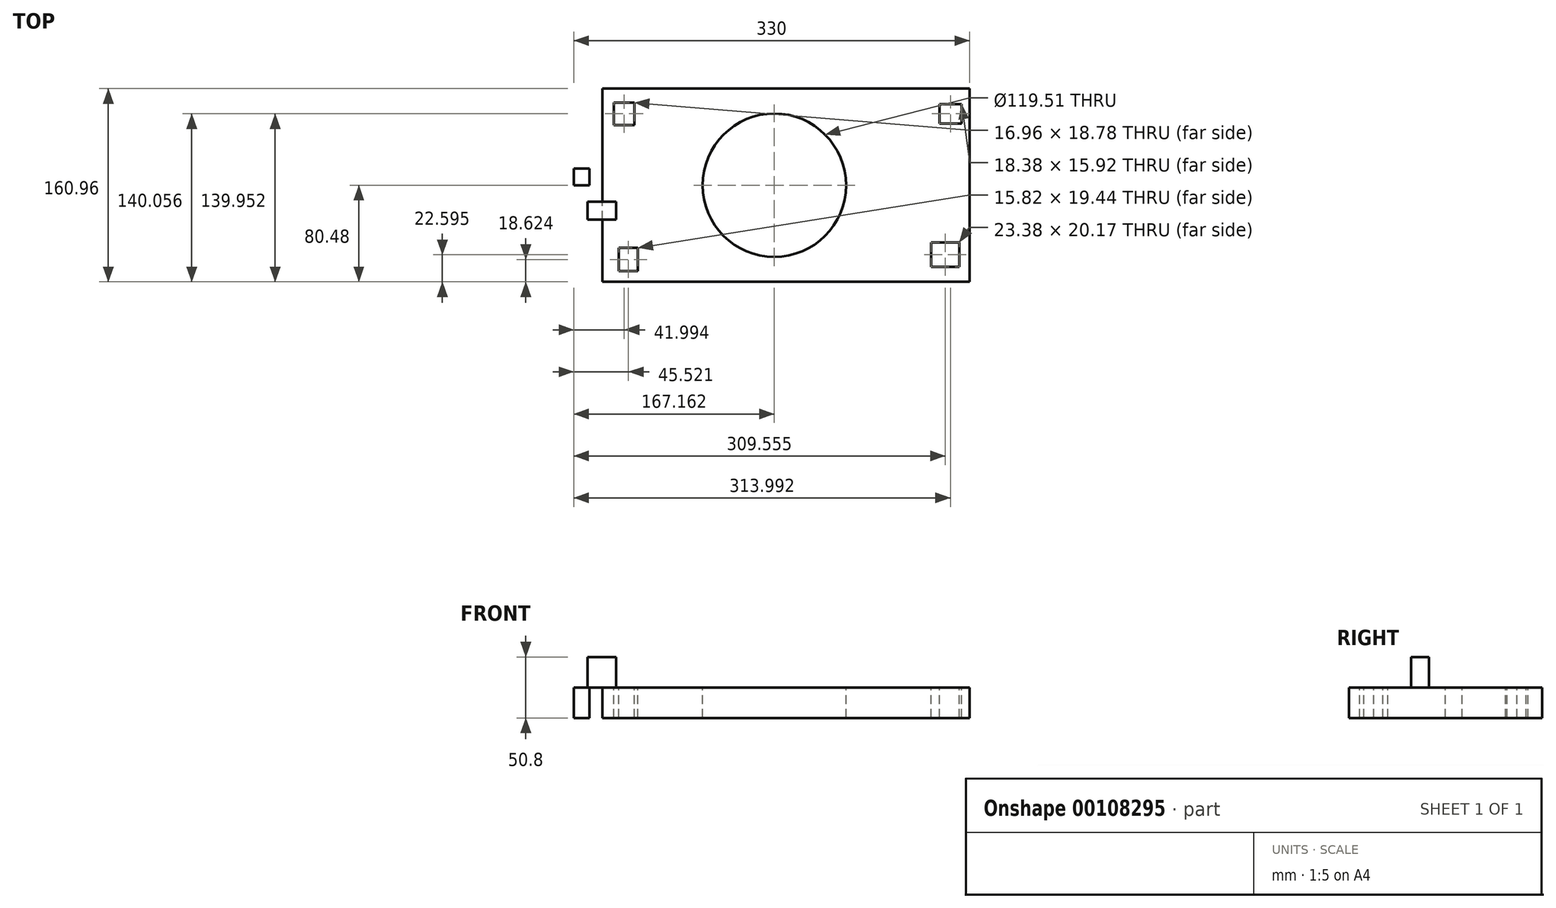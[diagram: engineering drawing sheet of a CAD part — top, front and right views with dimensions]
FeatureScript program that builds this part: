
annotation { "Feature Type Name" : "Feature", "Feature Type Description" : "" }
export const myFeature = defineFeature(function(context is Context, id is Id, definition is map)
    precondition{}
    {
        {
            var Q0;
            Q0=qCreatedBy(makeId("Top.planeOp"),FACE);
            var sketch = newSketch(context, id + "F0", { "sketchPlane" : qUnion([Q0])});
            skLineSegment(sketch, "E0.bottom", {"start": v(153.1, -80.48) * mm, "end": v(-153.1, -80.48) * mm});
            skLineSegment(sketch, "E0.top", {"start": v(153.1, 80.48) * mm, "end": v(-153.1, 80.48) * mm});
            skLineSegment(sketch, "E0.left", {"start": v(153.1, -80.48) * mm, "end": v(153.1, 80.48) * mm});
            skLineSegment(sketch, "E0.right", {"start": v(-153.1, -80.48) * mm, "end": v(-153.1, 80.48) * mm});
            skPoint(sketch, "E0.middle", {"position": v(0, 0) * mm});
            skSolve(sketch);
        }
        {
            var Q0;
            Q0 = qSketchRegion(id + "F0", true);
            extrude(context, id + "F1", {"entities" : qUnion([Q0]), "depth" : 25.4 * mm});
        }
        {
            var Q0;
            Q0=makeQuery(id+"F1.opExtrude","CAP_FACE",FACE,{"disambiguationData":[OSD([sQuery(id+"F0.wireOp",EDGE,"E0.bottom"),sQuery(id+"F0.wireOp",EDGE,"E0.top"),sQuery(id+"F0.wireOp",EDGE,"E0.left"),sQuery(id+"F0.wireOp",EDGE,"E0.right")])],"isStart":false});
            var sketch = newSketch(context, id + "F2", { "sketchPlane" : qUnion([Q0])});
            skLineSegment(sketch, "E1.bottom", {"start": v(-143.39, 68.97) * mm, "end": v(-126.42, 68.97) * mm});
            skLineSegment(sketch, "E1.top", {"start": v(-143.39, 50.19) * mm, "end": v(-126.42, 50.19) * mm});
            skLineSegment(sketch, "E1.left", {"start": v(-143.39, 68.97) * mm, "end": v(-143.39, 50.19) * mm});
            skLineSegment(sketch, "E1.right", {"start": v(-126.42, 68.97) * mm, "end": v(-126.42, 50.19) * mm});
            skLineSegment(sketch, "E2.bottom", {"start": v(127.9, 67.43) * mm, "end": v(146.28, 67.43) * mm});
            skLineSegment(sketch, "E2.top", {"start": v(127.9, 51.51) * mm, "end": v(146.28, 51.51) * mm});
            skLineSegment(sketch, "E2.left", {"start": v(127.9, 67.43) * mm, "end": v(127.9, 51.51) * mm});
            skLineSegment(sketch, "E2.right", {"start": v(146.28, 67.43) * mm, "end": v(146.28, 51.51) * mm});
            skLineSegment(sketch, "E3.bottom", {"start": v(-139.29, -52.14) * mm, "end": v(-123.47, -52.14) * mm});
            skLineSegment(sketch, "E3.top", {"start": v(-139.29, -71.58) * mm, "end": v(-123.47, -71.58) * mm});
            skLineSegment(sketch, "E3.left", {"start": v(-139.29, -52.14) * mm, "end": v(-139.29, -71.58) * mm});
            skLineSegment(sketch, "E3.right", {"start": v(-123.47, -52.14) * mm, "end": v(-123.47, -71.58) * mm});
            skSolve(sketch);
        }
        {
            var Q0;
            Q0 = qSketchRegion(id + "F2", true);
            extrude(context, id + "F3", {"entities" : qUnion([Q0]), "operationType" : NewBodyOperationType.REMOVE, "oppositeDirection" : true, "depth" : 25.4 * mm});
        }
        {
            var Q0;
            Q0=makeQuery(id+"F1.opExtrude","CAP_FACE",FACE,{"disambiguationData":[OSD([sQuery(id+"F0.wireOp",EDGE,"E0.bottom"),sQuery(id+"F0.wireOp",EDGE,"E0.top"),sQuery(id+"F0.wireOp",EDGE,"E0.left"),sQuery(id+"F0.wireOp",EDGE,"E0.right")])],"isStart":false});
            var sketch = newSketch(context, id + "F4", { "sketchPlane" : qUnion([Q0])});
            skLineSegment(sketch, "E4.bottom", {"start": v(120.96, -47.8) * mm, "end": v(144.35, -47.8) * mm});
            skLineSegment(sketch, "E4.top", {"start": v(120.96, -67.97) * mm, "end": v(144.35, -67.97) * mm});
            skLineSegment(sketch, "E4.left", {"start": v(120.96, -47.8) * mm, "end": v(120.96, -67.97) * mm});
            skLineSegment(sketch, "E4.right", {"start": v(144.35, -47.8) * mm, "end": v(144.35, -67.97) * mm});
            skSolve(sketch);
        }
        {
            var Q0;
            Q0 = qSketchRegion(id + "F4", true);
            extrude(context, id + "F5", {"entities" : qUnion([Q0]), "operationType" : NewBodyOperationType.REMOVE, "oppositeDirection" : true, "depth" : 25.4 * mm});
        }
        {
            var Q0;
            Q0=makeQuery(id+"F1.opExtrude","CAP_FACE",FACE,{"disambiguationData":[OSD([sQuery(id+"F0.wireOp",EDGE,"E0.bottom"),sQuery(id+"F0.wireOp",EDGE,"E0.top"),sQuery(id+"F0.wireOp",EDGE,"E0.left"),sQuery(id+"F0.wireOp",EDGE,"E0.right")])],"isStart":false});
            var sketch = newSketch(context, id + "F6", { "sketchPlane" : qUnion([Q0])});
            skLineSegment(sketch, "E5", {"start": v(-139.29, -61.86) * mm, "end": v(-165.4, -13.75) * mm});
            skLineSegment(sketch, "E6.bottom", {"start": v(-165.4, -13.75) * mm, "end": v(-141.78, -13.75) * mm});
            skLineSegment(sketch, "E6.top", {"start": v(-165.4, -28.68) * mm, "end": v(-141.78, -28.68) * mm});
            skLineSegment(sketch, "E6.left", {"start": v(-165.4, -13.75) * mm, "end": v(-165.4, -28.68) * mm});
            skLineSegment(sketch, "E6.right", {"start": v(-141.78, -13.75) * mm, "end": v(-141.78, -28.68) * mm});
            skSolve(sketch);
        }
        {
            var Q0;
            Q0 = qSketchRegion(id + "F6", true);
            extrude(context, id + "F7", {"entities" : qUnion([Q0]), "operationType" : NewBodyOperationType.ADD, "depth" : 25.4 * mm});
        }
        {
            var Q0;
            {var subQ4=makeQuery(id+"F1.opExtrude","CAP_EDGE",EDGE,{"disambiguationData":[OSD([sQuery(id+"F0.wireOp",EDGE,"E0.bottom")])],"isStart":false});Q0=makeQuery(id+"F6.imprint","IMPRINT",FACE,{"disambiguationData":[TD([[makeQuery(id+"F6.imprint","IMPRINT",EDGE,{"derivedFrom":subQ4}),-1.0]])]});}
            var sketch = newSketch(context, id + "F8", { "sketchPlane" : qUnion([Q0])});
            skLineSegment(sketch, "E7.bottom", {"start": v(-176.9, 13.9) * mm, "end": v(-163.88, 13.9) * mm});
            skLineSegment(sketch, "E7.top", {"start": v(-176.9, 0) * mm, "end": v(-163.88, 0) * mm});
            skLineSegment(sketch, "E7.left", {"start": v(-176.9, 13.9) * mm, "end": v(-176.9, 0) * mm});
            skLineSegment(sketch, "E7.right", {"start": v(-163.88, 13.9) * mm, "end": v(-163.88, 0) * mm});
            skSolve(sketch);
        }
        {
            var Q0;
            Q0 = qSketchRegion(id + "F8", true);
            extrude(context, id + "F9", {"entities" : qUnion([Q0]), "operationType" : NewBodyOperationType.ADD, "oppositeDirection" : true, "depth" : 25.4 * mm});
        }
        {
            var Q0;
            Q0=qCreatedBy(makeId("Right.planeOp"),FACE);
            var sketch = newSketch(context, id + "F10", { "sketchPlane" : qUnion([Q0])});
            skLineSegment(sketch, "E8.bottom", {"start": v(195.7, -224.48) * mm, "end": v(352.54, -224.48) * mm});
            skLineSegment(sketch, "E8.top", {"start": v(195.7, -96.3) * mm, "end": v(352.54, -96.3) * mm});
            skLineSegment(sketch, "E8.left", {"start": v(195.7, -224.48) * mm, "end": v(195.7, -96.3) * mm});
            skLineSegment(sketch, "E8.right", {"start": v(352.54, -224.48) * mm, "end": v(352.54, -96.3) * mm});
            skLineSegment(sketch, "E9.bottom", {"start": v(-353.36, 280.55) * mm, "end": v(-197.63, 280.55) * mm});
            skLineSegment(sketch, "E9.top", {"start": v(-353.36, 289.92) * mm, "end": v(-197.63, 289.92) * mm});
            skLineSegment(sketch, "E9.left", {"start": v(-353.36, 280.55) * mm, "end": v(-353.36, 289.92) * mm});
            skLineSegment(sketch, "E9.right", {"start": v(-197.63, 280.55) * mm, "end": v(-197.63, 289.92) * mm});
            skSolve(sketch);
        }
        {
            var Q0;
            Q0 = qSketchRegion(id + "F10", true);
            extrude(context, id + "F11", {"entities" : qUnion([Q0]), "operationType" : NewBodyOperationType.REMOVE, "oppositeDirection" : true, "depth" : 25.4 * mm});
        }
        {
            var Q0;
            Q0=makeQuery(id+"F1.opExtrude","CAP_FACE",FACE,{"disambiguationData":[OSD([sQuery(id+"F0.wireOp",EDGE,"E0.bottom"),sQuery(id+"F0.wireOp",EDGE,"E0.top"),sQuery(id+"F0.wireOp",EDGE,"E0.left"),sQuery(id+"F0.wireOp",EDGE,"E0.right")])],"isStart":false});
            var sketch = newSketch(context, id + "F12", { "sketchPlane" : qUnion([Q0])});
            skCircle(sketch, "E10", {"center": v(-9.74, 0) * mm, "radius": 59.75 * mm});
            skSolve(sketch);
        }
        {
            var Q0;
            Q0 = qSketchRegion(id + "F12", true);
            extrude(context, id + "F13", {"entities" : qUnion([Q0]), "operationType" : NewBodyOperationType.REMOVE, "oppositeDirection" : true, "depth" : 25.4 * mm});
        }
    });
